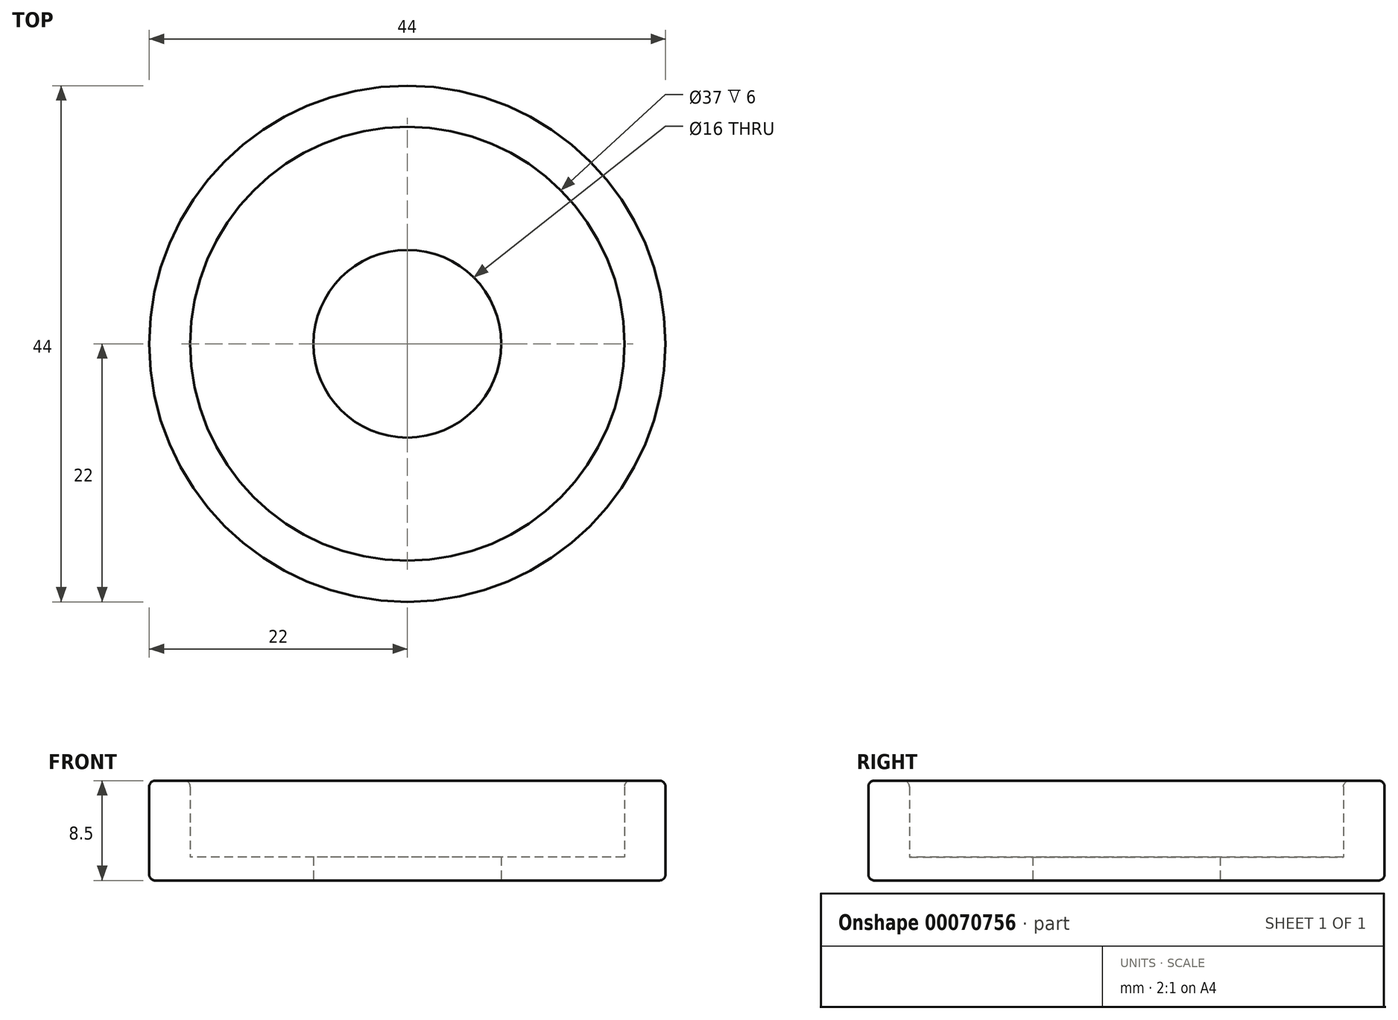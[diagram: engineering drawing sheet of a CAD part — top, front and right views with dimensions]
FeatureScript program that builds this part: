
annotation { "Feature Type Name" : "Feature", "Feature Type Description" : "" }
export const myFeature = defineFeature(function(context is Context, id is Id, definition is map)
    precondition{}
    {
        {
            var Q0;
            Q0=qCreatedBy(makeId("Top.planeOp"),FACE);
            var sketch = newSketch(context, id + "F0", { "sketchPlane" : qUnion([Q0])});
            skCircle(sketch, "E0", {"center": v(0, 0) * mm, "radius": 18.5 * mm});
            skCircle(sketch, "E1", {"center": v(0, 0) * mm, "radius": 22 * mm});
            skCircle(sketch, "E2", {"center": v(0, 0) * mm, "radius": 8 * mm});
            skSolve(sketch);
        }
        {
            var Q0;
            Q0 = qSketchRegion(id + "F0", true);
            extrude(context, id + "F1", {"entities" : qUnion([Q0]), "depth" : 8.5 * mm});
        }
        {
            var Q0;
            Q0=makeQuery(id+"F0.imprint","IMPRINT",FACE,{"disambiguationData":[TD([[makeQuery(id+"F0.imprint","IMPRINT",EDGE,{"derivedFrom":sQuery(id+"F0.wireOp",EDGE,"E0")}),1.0]])]});
            extrude(context, id + "F2", {"entities" : qUnion([Q0]), "operationType" : NewBodyOperationType.ADD, "depth" : 2 * mm});
        }
        {
            var Q0;
            Q0=makeQuery(id+"F1.opExtrude","CAP_EDGE",EDGE,{"disambiguationData":[OSD([sQuery(id+"F0.wireOp",EDGE,"E1")])],"isStart":false});
            var Q1;
            Q1=makeQuery(id+"F1.opExtrude","CAP_EDGE",EDGE,{"disambiguationData":[OSD([sQuery(id+"F0.wireOp",EDGE,"E1")])],"isStart":true});
            var Q2;
            Q2=makeQuery(id+"F1.opExtrude","CAP_EDGE",EDGE,{"disambiguationData":[OSD([sQuery(id+"F0.wireOp",EDGE,"E0")])],"isStart":false});
            fillet(context, id + "F3", {"entities" : qUnion([Q0, Q1, Q2]), "radius" : .5 * mm, "tangentPropagation" : true, "allowEdgeOverflow" : false});
        }
    });
